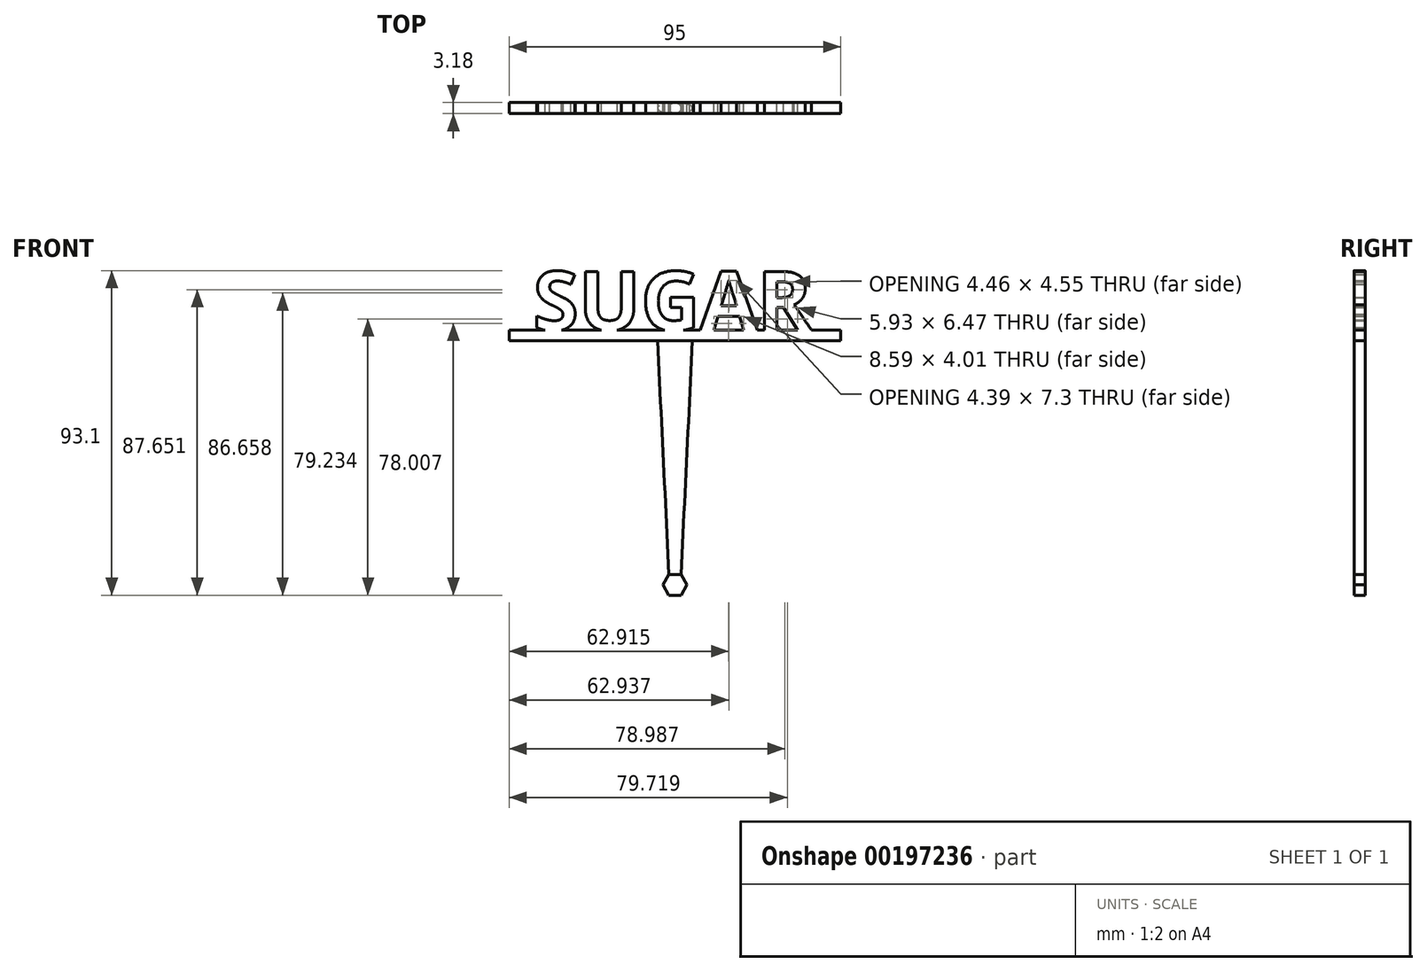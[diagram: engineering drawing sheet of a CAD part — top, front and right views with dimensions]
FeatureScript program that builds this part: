
annotation { "Feature Type Name" : "Feature", "Feature Type Description" : "" }
export const myFeature = defineFeature(function(context is Context, id is Id, definition is map)
    precondition{}
    {
        {
            var Q0;
            Q0=qCreatedBy(makeId("Front.planeOp"),FACE);
            var sketch = newSketch(context, id + "F0", { "sketchPlane" : qUnion([Q0])});
            skLineSegment(sketch, "E0.bottom", {"start": v(-47.5, 3) * mm, "end": v(47.5, 3) * mm});
            skLineSegment(sketch, "E0.top", {"start": v(-47.5, 0) * mm, "end": v(47.5, 0) * mm});
            skLineSegment(sketch, "E0.left", {"start": v(-47.5, 3) * mm, "end": v(-47.5, 0) * mm});
            skLineSegment(sketch, "E0.right", {"start": v(47.5, 3) * mm, "end": v(47.5, 0) * mm});
            skText(sketch, "E1", { "text": "SUGAR", "fontName": "OpenSans-Bold.ttf"});
            const initialGuessF0  = {"E1": [-0.04068, 0.003, 1, 0, 0.017]};
            skSetInitialGuess(sketch, initialGuessF0);
            skSolve(sketch);
        }
        {
            var Q0;
            Q0=qSketchRegion(id+"F0",true);
            extrude(context, id + "F1", {"entities" : qUnion([Q0]), "depth" : 3.17 * mm});
        }
        {
            var Q0;
            Q0=qCreatedBy(makeId("Top.planeOp"),FACE);
            var sketch = newSketch(context, id + "F2", { "sketchPlane" : qUnion([Q0])});
            skLineSegment(sketch, "E2.bottom", {"start": v(0, 0) * mm, "end": v(2.5, 0) * mm, "construction": true});
            skLineSegment(sketch, "E2.top", {"start": v(0, -3.17) * mm, "end": v(2.5, -3.17) * mm, "construction": true});
            skLineSegment(sketch, "E2.left", {"start": v(0, 0) * mm, "end": v(0, -3.18) * mm, "construction": true});
            skLineSegment(sketch, "E2.right", {"start": v(2.5, 0) * mm, "end": v(2.5, -3.17) * mm, "construction": true});
            skEllipse(sketch, "E3", {"center": v(0, -1.59) * mm, "majorRadius": 5 * mm, "minorRadius": 1.59 * mm, "majorAxis": v(1, 0)});
            skSolve(sketch);
        }
        {
            var Q0;
            Q0=qCreatedBy(makeId("Top.planeOp"),FACE);
            cPlane(context, id + "F3", {"entities" : qUnion([Q0]), "cplaneType" : CPlaneType.OFFSET, "offset" : 70 * mm, "oppositeDirection" : true, "width" : 150 * mm, "height" : 150 * mm});
        }
        {
            var Q0;
            Q0=qCreatedBy(id+"F3.planeOp",FACE);
            var sketch = newSketch(context, id + "F4", { "sketchPlane" : qUnion([Q0])});
            skPoint(sketch, "E4", {"position": v(0, 0) * mm});
            skLineSegment(sketch, "E5.0", {"start": v(-50.9, -1.59) * mm, "end": v(49.1, -1.59) * mm, "construction": true});
            skLineSegment(sketch, "E6.0", {"start": v(0, 0) * mm, "end": v(0, -3.17) * mm, "construction": true});
            skCircle(sketch, "E7", {"center": v(0, -1.59) * mm, "radius": 1.59 * mm});
            skSolve(sketch);
        }
        {
            var Q1;
            Q1=makeQuery(id+"F2.imprint","IMPRINT",FACE,{"disambiguationData":[TD([[makeQuery(id+"F2.imprint","IMPRINT",EDGE,{"derivedFrom":sQuery(id+"F2.wireOp",EDGE,"E3")}),1.0]])]});
            var Q2;
            Q2=makeQuery(id+"F4.imprint","IMPRINT",FACE,{"disambiguationData":[TD([[makeQuery(id+"F4.imprint","IMPRINT",EDGE,{"derivedFrom":sQuery(id+"F4.wireOp",EDGE,"E7")}),1.0]])]});
            loft(context, id + "F5", {"operationType" : NewBodyOperationType.ADD, "sheetProfilesArray" : [{ "sheetProfileEntities" : qUnion([Q1]) }, { "sheetProfileEntities" : qUnion([Q2]) }]});
        }
        {
            var Q0;
            Q0=qCreatedBy(makeId("Front.planeOp"),FACE);
            var sketch = newSketch(context, id + "F6", { "sketchPlane" : qUnion([Q0])});
            skLineSegment(sketch, "E8.bottom", {"start": v(3, -73) * mm, "end": v(-3, -73) * mm, "construction": true});
            skLineSegment(sketch, "E8.top", {"start": v(3, -67) * mm, "end": v(-3, -67) * mm, "construction": true});
            skLineSegment(sketch, "E8.left", {"start": v(3, -73) * mm, "end": v(3, -67) * mm, "construction": true});
            skLineSegment(sketch, "E8.right", {"start": v(-3, -73) * mm, "end": v(-3, -67) * mm, "construction": true});
            skPoint(sketch, "E8.middle", {"position": v(0, -70) * mm});
            skCircle(sketch, "E9.cCircle", {"center": v(0, -70) * mm, "radius": 3 * mm, "construction": true});
            skLineSegment(sketch, "E9.0", {"start": v(0, -73) * mm, "end": v(-2.6, -71.5) * mm, "construction": true});
            skLineSegment(sketch, "E9.1", {"start": v(-2.6, -71.5) * mm, "end": v(-2.6, -68.5) * mm, "construction": true});
            skLineSegment(sketch, "E9.2", {"start": v(-2.6, -68.5) * mm, "end": v(0, -67) * mm, "construction": true});
            skLineSegment(sketch, "E9.3", {"start": v(0, -67) * mm, "end": v(2.6, -68.5) * mm, "construction": true});
            skLineSegment(sketch, "E9.4", {"start": v(2.6, -68.5) * mm, "end": v(2.6, -71.5) * mm, "construction": true});
            skLineSegment(sketch, "E9.5", {"start": v(2.6, -71.5) * mm, "end": v(0, -73) * mm, "construction": true});
            skLineSegment(sketch, "E10.0", {"start": v(1.73, -73) * mm, "end": v(-1.73, -73) * mm});
            skLineSegment(sketch, "E10.1", {"start": v(-1.73, -73) * mm, "end": v(-3.46, -70) * mm});
            skLineSegment(sketch, "E10.2", {"start": v(-3.46, -70) * mm, "end": v(-1.73, -67) * mm});
            skLineSegment(sketch, "E10.3", {"start": v(-1.73, -67) * mm, "end": v(1.73, -67) * mm});
            skLineSegment(sketch, "E10.4", {"start": v(1.73, -67) * mm, "end": v(3.46, -70) * mm});
            skLineSegment(sketch, "E10.5", {"start": v(3.46, -70) * mm, "end": v(1.73, -73) * mm});
            skPoint(sketch, "E10.0.midPoint", {"position": v(0, -73) * mm});
            skSolve(sketch);
        }
        {
            var Q0;
            Q0=makeQuery(id+"F6.imprint","IMPRINT",FACE,{"disambiguationData":[TD([[makeQuery(id+"F6.imprint","IMPRINT",EDGE,{"derivedFrom":sQuery(id+"F6.wireOp",EDGE,"E10.0")}),-1.0]])]});
            extrude(context, id + "F7", {"entities" : qUnion([Q0]), "operationType" : NewBodyOperationType.ADD, "depth" : 3.17 * mm});
        }
    });
